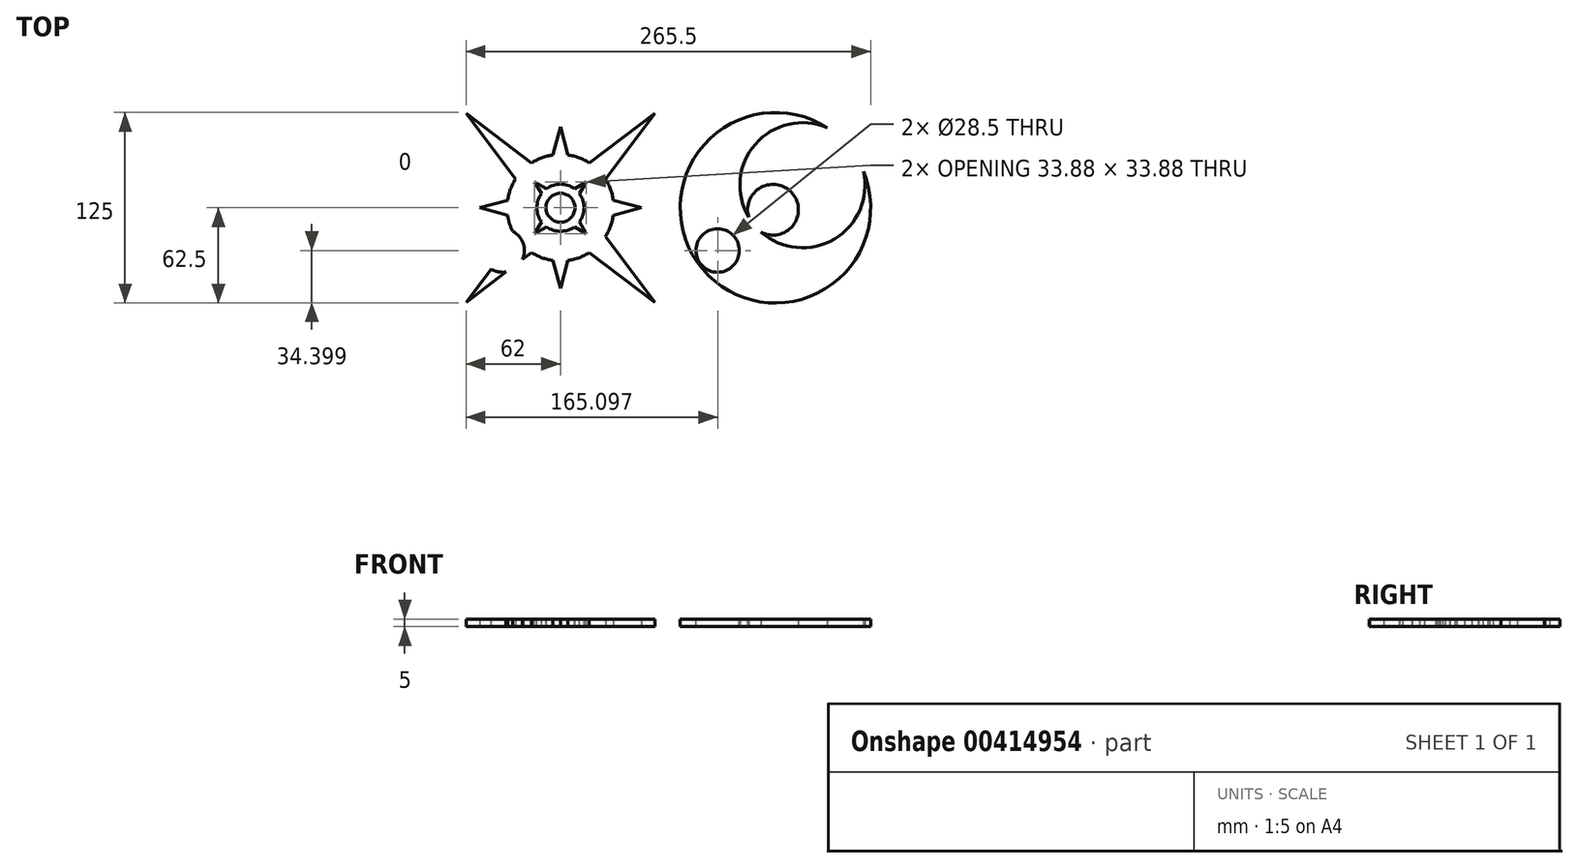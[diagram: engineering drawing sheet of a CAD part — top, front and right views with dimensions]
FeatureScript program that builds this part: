
annotation { "Feature Type Name" : "Feature", "Feature Type Description" : "" }
export const myFeature = defineFeature(function(context is Context, id is Id, definition is map)
    precondition{}
    {
        {
            var Q0;
            Q0=qCreatedBy(makeId("Top.planeOp"),FACE);
            var sketch = newSketch(context, id + "F0", { "sketchPlane" : qUnion([Q0])});
            skArc(sketch, "E0", {"start": v(-4.93, 34.65) * mm, "mid": v(-24.75, 24.75) * mm, "end": v(-34.65, 4.93) * mm});
            skLineSegment(sketch, "E1", {"start": v(-4.93, 34.65) * mm, "end": v(0, 53) * mm});
            skLineSegment(sketch, "E2", {"start": v(-53, 0) * mm, "end": v(-34.65, 4.93) * mm});
            skLineSegment(sketch, "E3.MirrorCS", {"start": v(-4.93, -34.65) * mm, "end": v(0, -53) * mm});
            skLineSegment(sketch, "E4.MirrorCS", {"start": v(-53, 0) * mm, "end": v(-34.65, -4.93) * mm});
            skLineSegment(sketch, "E5.MirrorCS", {"start": v(4.93, 34.65) * mm, "end": v(0, 53) * mm});
            skLineSegment(sketch, "E6.MirrorCS", {"start": v(4.93, -34.65) * mm, "end": v(0, -53) * mm});
            skLineSegment(sketch, "E7.MirrorCS", {"start": v(53, 0) * mm, "end": v(34.65, 4.93) * mm});
            skLineSegment(sketch, "E8.MirrorCS", {"start": v(53, 0) * mm, "end": v(34.65, -4.93) * mm});
            skArc(sketch, "E9.trimOffspring", {"start": v(34.65, 4.93) * mm, "mid": v(24.75, 24.75) * mm, "end": v(4.93, 34.65) * mm});
            skArc(sketch, "E10.trimOffspring", {"start": v(-34.65, -4.93) * mm, "mid": v(-24.75, -24.75) * mm, "end": v(-4.93, -34.65) * mm});
            skArc(sketch, "E11.trimOffspring", {"start": v(4.93, -34.65) * mm, "mid": v(24.75, -24.75) * mm, "end": v(34.65, -4.93) * mm});
            skSolve(sketch);
        }
        {
            var Q0;
            Q0=makeQuery(id+"F0.imprint","IMPRINT",FACE,{"disambiguationData":[TD([[makeQuery(id+"F0.imprint","IMPRINT",EDGE,{"derivedFrom":sQuery(id+"F0.wireOp",EDGE,"E0")}),1.0]])]});
            var sketch = newSketch(context, id + "F1", { "sketchPlane" : qUnion([Q0])});
            skPoint(sketch, "E12.middle", {"position": v(0, 0) * mm});
            skLineSegment(sketch, "E13", {"start": v(-62, 62) * mm, "end": v(-29.45, 18.91) * mm});
            skLineSegment(sketch, "E14", {"start": v(-62, -62) * mm, "end": v(-18.91, -29.45) * mm});
            skLineSegment(sketch, "E15.MirrorCS", {"start": v(-62, 62) * mm, "end": v(-18.91, 29.45) * mm});
            skLineSegment(sketch, "E16.MirrorCS", {"start": v(62, 62) * mm, "end": v(29.45, 18.91) * mm});
            skLineSegment(sketch, "E17.MirrorCS", {"start": v(62, 62) * mm, "end": v(18.91, 29.45) * mm});
            skLineSegment(sketch, "E18.MirrorCS", {"start": v(-62, -62) * mm, "end": v(-29.45, -18.91) * mm});
            skLineSegment(sketch, "E19.MirrorCS", {"start": v(62, -62) * mm, "end": v(18.91, -29.45) * mm});
            skLineSegment(sketch, "E20.MirrorCS", {"start": v(62, -62) * mm, "end": v(29.45, -18.91) * mm});
            skSolve(sketch);
        }
        {
            var Q0;
            Q0=makeQuery(id+"F0.imprint","IMPRINT",FACE,{"disambiguationData":[TD([[makeQuery(id+"F0.imprint","IMPRINT",EDGE,{"derivedFrom":sQuery(id+"F0.wireOp",EDGE,"E0")}),1.0]])]});
            var Q1;
            {var subQ0=sQuery(id+"F1.wireOp",EDGE,"E13");Q1=makeQuery(id+"F1.imprint","IMPRINT",FACE,{"disambiguationData":[TD([[makeQuery(id+"F1.imprint","IMPRINT",EDGE,{"derivedFrom":subQ0}),1.0]])]});}
            var Q2;
            {var subQ0=sQuery(id+"F1.wireOp",EDGE,"E14");Q2=makeQuery(id+"F1.imprint","IMPRINT",FACE,{"disambiguationData":[TD([[makeQuery(id+"F1.imprint","IMPRINT",EDGE,{"derivedFrom":subQ0}),1.0]])]});}
            var Q3;
            {var subQ0=sQuery(id+"F1.wireOp",EDGE,"E19.MirrorCS");Q3=makeQuery(id+"F1.imprint","IMPRINT",FACE,{"disambiguationData":[TD([[makeQuery(id+"F1.imprint","IMPRINT",EDGE,{"derivedFrom":subQ0}),-1.0]])]});}
            var Q4;
            {var subQ0=sQuery(id+"F1.wireOp",EDGE,"E16.MirrorCS");Q4=makeQuery(id+"F1.imprint","IMPRINT",FACE,{"disambiguationData":[TD([[makeQuery(id+"F1.imprint","IMPRINT",EDGE,{"derivedFrom":subQ0}),-1.0]])]});}
            extrude(context, id + "F2", {"entities" : qUnion([Q0, Q1, Q2, Q3, Q4]), "depth" : 5 * mm});
        }
        {
            var Q0;
            Q0=makeQuery(id+"F2.opExtrude","SWEPT_BODY",BODY,{"disambiguationData":[OSD([sQuery(id+"F0.wireOp",EDGE,"E0"),sQuery(id+"F0.wireOp",EDGE,"E1"),sQuery(id+"F0.wireOp",EDGE,"E2"),sQuery(id+"F0.wireOp",EDGE,"E3.MirrorCS"),sQuery(id+"F0.wireOp",EDGE,"E4.MirrorCS"),sQuery(id+"F0.wireOp",EDGE,"E5.MirrorCS"),sQuery(id+"F0.wireOp",EDGE,"E6.MirrorCS"),sQuery(id+"F0.wireOp",EDGE,"E7.MirrorCS"),sQuery(id+"F0.wireOp",EDGE,"E8.MirrorCS"),sQuery(id+"F0.wireOp",EDGE,"E9.trimOffspring"),sQuery(id+"F0.wireOp",EDGE,"E10.trimOffspring"),sQuery(id+"F0.wireOp",EDGE,"E11.trimOffspring")])]});
            var Q1;
            Q1=makeQuery(id+"F2.opExtrude","SWEPT_BODY",BODY,{"disambiguationData":[OSD([sQuery(id+"F0.wireOp",EDGE,"E0"),sQuery(id+"F1.wireOp",EDGE,"E13"),sQuery(id+"F1.wireOp",EDGE,"E15.MirrorCS")])]});
            var Q2;
            Q2=makeQuery(id+"F2.opExtrude","SWEPT_BODY",BODY,{"disambiguationData":[OSD([sQuery(id+"F0.wireOp",EDGE,"E9.trimOffspring"),sQuery(id+"F1.wireOp",EDGE,"E16.MirrorCS"),sQuery(id+"F1.wireOp",EDGE,"E17.MirrorCS")])]});
            var Q3;
            Q3=makeQuery(id+"F2.opExtrude","SWEPT_BODY",BODY,{"disambiguationData":[OSD([sQuery(id+"F0.wireOp",EDGE,"E11.trimOffspring"),sQuery(id+"F1.wireOp",EDGE,"E19.MirrorCS"),sQuery(id+"F1.wireOp",EDGE,"E20.MirrorCS")])]});
            var Q4;
            Q4=makeQuery(id+"F2.opExtrude","SWEPT_BODY",BODY,{"disambiguationData":[OSD([sQuery(id+"F0.wireOp",EDGE,"E10.trimOffspring"),sQuery(id+"F1.wireOp",EDGE,"E14"),sQuery(id+"F1.wireOp",EDGE,"E18.MirrorCS")])]});
            booleanBodies(context, id + "F3", {"operationType" : BooleanOperationType.UNION, "tools" : qUnion([Q0, Q1, Q2, Q3, Q4])});
        }
        {
            var Q0;
            {var subQ0=sQuery(id+"F0.wireOp",EDGE,"E11.trimOffspring");var subQ1=sQuery(id+"F0.wireOp",EDGE,"E9.trimOffspring");var subQ2=sQuery(id+"F0.wireOp",EDGE,"E10.trimOffspring");var subQ3=sQuery(id+"F0.wireOp",EDGE,"E0");Q0=makeQuery(id+"F3.opBoolean","MERGE",FACE,{"derivedFrom":[makeQuery(id+"F2.opExtrude","CAP_FACE",FACE,{"disambiguationData":[OSD([subQ3,sQuery(id+"F0.wireOp",EDGE,"E1"),sQuery(id+"F0.wireOp",EDGE,"E2"),sQuery(id+"F0.wireOp",EDGE,"E3.MirrorCS"),sQuery(id+"F0.wireOp",EDGE,"E4.MirrorCS"),sQuery(id+"F0.wireOp",EDGE,"E5.MirrorCS"),sQuery(id+"F0.wireOp",EDGE,"E6.MirrorCS"),sQuery(id+"F0.wireOp",EDGE,"E7.MirrorCS"),sQuery(id+"F0.wireOp",EDGE,"E8.MirrorCS"),subQ1,subQ2,subQ0])],"isStart":false}),makeQuery(id+"F2.opExtrude","CAP_FACE",FACE,{"disambiguationData":[OSD([subQ3,sQuery(id+"F1.wireOp",EDGE,"E13"),sQuery(id+"F1.wireOp",EDGE,"E15.MirrorCS")])],"isStart":false}),makeQuery(id+"F2.opExtrude","CAP_FACE",FACE,{"disambiguationData":[OSD([subQ2,sQuery(id+"F1.wireOp",EDGE,"E14"),sQuery(id+"F1.wireOp",EDGE,"E18.MirrorCS")])],"isStart":false}),makeQuery(id+"F2.opExtrude","CAP_FACE",FACE,{"disambiguationData":[OSD([subQ1,sQuery(id+"F1.wireOp",EDGE,"E16.MirrorCS"),sQuery(id+"F1.wireOp",EDGE,"E17.MirrorCS")])],"isStart":false}),makeQuery(id+"F2.opExtrude","CAP_FACE",FACE,{"disambiguationData":[OSD([subQ0,sQuery(id+"F1.wireOp",EDGE,"E19.MirrorCS"),sQuery(id+"F1.wireOp",EDGE,"E20.MirrorCS")])],"isStart":false})]});}
            var sketch = newSketch(context, id + "F4", { "sketchPlane" : qUnion([Q0])});
            skCircle(sketch, "E21", {"center": v(0, 0) * mm, "radius": 9.5 * mm});
            skArc(sketch, "E22", {"start": v(9.22, 12.46) * mm, "mid": v(0, 15.5) * mm, "end": v(-9.22, 12.46) * mm});
            skLineSegment(sketch, "E23", {"start": v(-17.44, 17.23) * mm, "end": v(-9.22, 12.46) * mm});
            skLineSegment(sketch, "E24", {"start": v(17.23, 17.44) * mm, "end": v(12.46, 9.22) * mm});
            skLineSegment(sketch, "E25.MirrorCS", {"start": v(17.44, 17.23) * mm, "end": v(9.22, 12.46) * mm});
            skLineSegment(sketch, "E26.MirrorCS", {"start": v(17.23, -17.44) * mm, "end": v(12.46, -9.22) * mm});
            skLineSegment(sketch, "E27.MirrorCS", {"start": v(-17.23, 17.44) * mm, "end": v(-12.46, 9.22) * mm});
            skLineSegment(sketch, "E28.MirrorCS", {"start": v(17.44, -17.23) * mm, "end": v(9.22, -12.46) * mm});
            skLineSegment(sketch, "E29.MirrorCS", {"start": v(-17.23, -17.44) * mm, "end": v(-12.46, -9.22) * mm});
            skLineSegment(sketch, "E30.MirrorCS", {"start": v(-17.44, -17.23) * mm, "end": v(-9.22, -12.46) * mm});
            skArc(sketch, "E31.trimOffspring", {"start": v(-12.46, 9.22) * mm, "mid": v(-15.5, 0) * mm, "end": v(-12.46, -9.22) * mm});
            skArc(sketch, "E32.trimOffspring", {"start": v(-9.22, -12.46) * mm, "mid": v(0, -15.5) * mm, "end": v(9.22, -12.46) * mm});
            skArc(sketch, "E33.trimOffspring", {"start": v(12.46, -9.22) * mm, "mid": v(15.5, 0) * mm, "end": v(12.46, 9.22) * mm});
            skLineSegment(sketch, "E34", {"start": v(0, 15.5) * mm, "end": v(0, 9.5) * mm, "construction": true});
            skSolve(sketch);
        }
        {
            var Q0;
            Q0=makeQuery(id+"F4.imprint","IMPRINT",FACE,{"disambiguationData":[TD([[makeQuery(id+"F4.imprint","IMPRINT",EDGE,{"derivedFrom":sQuery(id+"F4.wireOp",EDGE,"E21")}),-1.0]])]});
            extrude(context, id + "F5", {"entities" : qUnion([Q0]), "operationType" : NewBodyOperationType.REMOVE, "oppositeDirection" : true, "depth" : 25 * mm});
        }
        {
            var Q0;
            Q0=qCreatedBy(makeId("Top.planeOp"),FACE);
            var sketch = newSketch(context, id + "F6", { "sketchPlane" : qUnion([Q0])});
            skArc(sketch, "E35", {"start": v(33.99, 52.45) * mm, "mid": v(-46.78, 41.45) * mm, "end": v(-47.98, -40.05) * mm});
            skArc(sketch, "E36", {"start": v(33.99, 52.45) * mm, "mid": v(-13.8, -11.49) * mm, "end": v(57.76, 23.88) * mm});
            skLineSegment(sketch, "E37", {"start": v(0, 0) * mm, "end": v(-47.98, -40.05) * mm, "construction": true});
            skArc(sketch, "E38.trimOffspring", {"start": v(-47.73, -40.34) * mm, "mid": v(32.5, -53.39) * mm, "end": v(57.76, 23.88) * mm});
            skCircle(sketch, "E39", {"center": v(-1.58, -1.32) * mm, "radius": 16.66 * mm});
            skLineSegment(sketch, "E40", {"start": v(-47.98, -40.05) * mm, "end": v(-47.73, -40.34) * mm});
            skSolve(sketch);
        }
        {
            var Q0;
            Q0=makeQuery(id+"F6.imprint","IMPRINT",FACE,{"disambiguationData":[TD([[makeQuery(id+"F6.imprint","IMPRINT",EDGE,{"derivedFrom":sQuery(id+"F6.wireOp",EDGE,"E39")}),1.0]])]});
            var Q1;
            {var subQ0=sQuery(id+"F6.wireOp",EDGE,"E36");Q1=makeQuery(id+"F6.imprint","IMPRINT",FACE,{"disambiguationData":[TD([[makeQuery(id+"F6.imprint","IMPRINT",EDGE,{"derivedFrom":subQ0}),-1.0]])]});}
            extrude(context, id + "F7", {"entities" : qUnion([Q0, Q1]), "depth" : 5 * mm});
        }
        {
            var Q0;
            Q0=makeQuery(id+"F7.opExtrude","CAP_FACE",FACE,{"disambiguationData":[OSD([sQuery(id+"F6.wireOp",EDGE,"E35"),sQuery(id+"F6.wireOp",EDGE,"E36"),sQuery(id+"F6.wireOp",EDGE,"E38.trimOffspring"),sQuery(id+"F6.wireOp",EDGE,"E39"),sQuery(id+"F6.wireOp",EDGE,"E40")])],"isStart":false});
            var sketch = newSketch(context, id + "F8", { "sketchPlane" : qUnion([Q0])});
            skLineSegment(sketch, "E41", {"start": v(0, 0) * mm, "end": v(-50.2, -37.22) * mm, "construction": true});
            skCircle(sketch, "E42", {"center": v(-37.9, -28.1) * mm, "radius": 14.25 * mm});
            skSolve(sketch);
        }
        {
            var Q0;
            Q0=makeQuery(id+"F8.imprint","IMPRINT",FACE,{"disambiguationData":[TD([[makeQuery(id+"F8.imprint","IMPRINT",EDGE,{"derivedFrom":sQuery(id+"F8.wireOp",EDGE,"E42")}),1.0]])]});
            extrude(context, id + "F9", {"entities" : qUnion([Q0]), "operationType" : NewBodyOperationType.REMOVE, "oppositeDirection" : true, "depth" : 25 * mm});
        }
        {
            var Q0;
            Q0=makeQuery(id+"F7.opExtrude","SWEPT_BODY",BODY,{"disambiguationData":[OSD([sQuery(id+"F6.wireOp",EDGE,"E35"),sQuery(id+"F6.wireOp",EDGE,"E36"),sQuery(id+"F6.wireOp",EDGE,"E38.trimOffspring"),sQuery(id+"F6.wireOp",EDGE,"E39"),sQuery(id+"F6.wireOp",EDGE,"E40")])]});
            transform(context, id + "F10", {"entities" : qUnion([Q0]), "transformType" : TransformType.TRANSLATION_3D, "dx" : 141 * mm, "dy" : 0 * mm, "dz" : 0 * mm, "makeCopy" : false});
        }
    });
